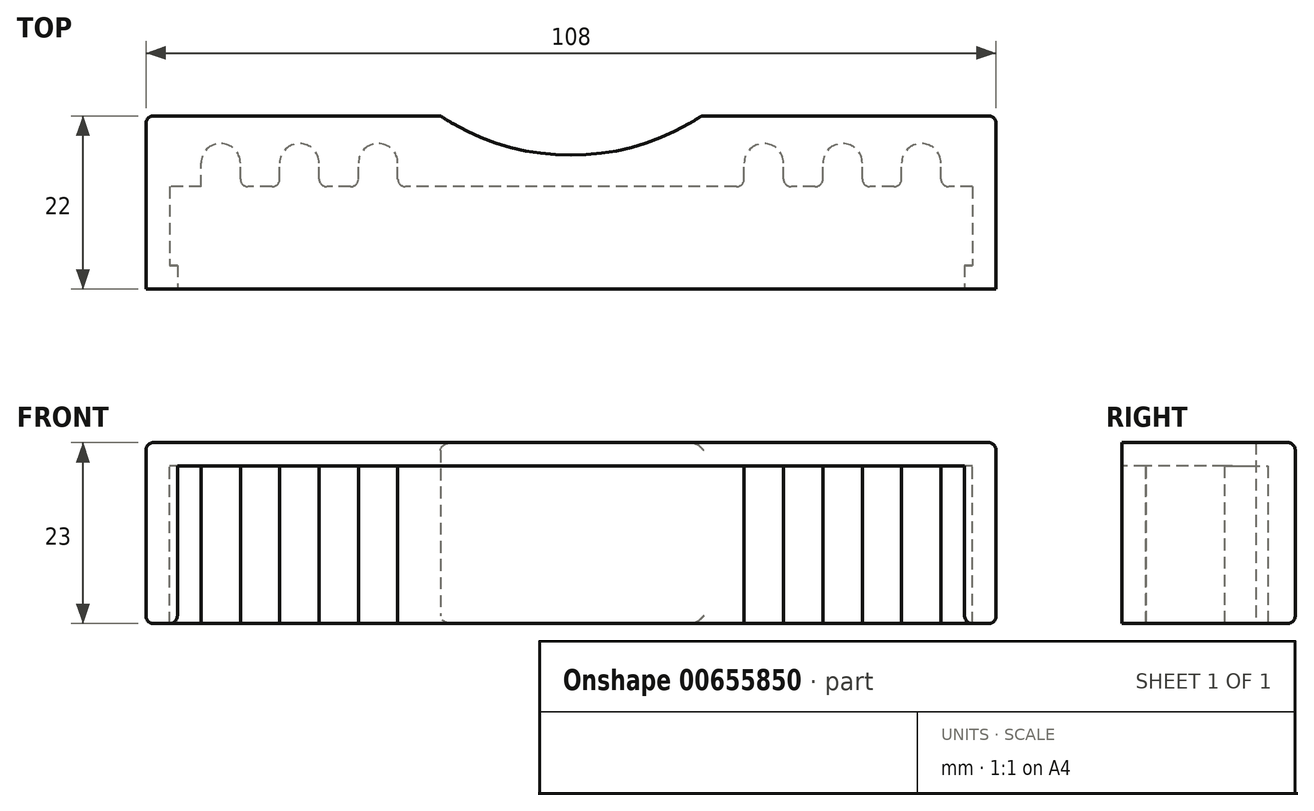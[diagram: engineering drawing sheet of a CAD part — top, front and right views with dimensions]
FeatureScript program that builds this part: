
annotation { "Feature Type Name" : "Feature", "Feature Type Description" : "" }
export const myFeature = defineFeature(function(context is Context, id is Id, definition is map)
    precondition{}
    {
        {
            var Q0;
            Q0=qCreatedBy(makeId("Front.planeOp"),FACE);
            var sketch = newSketch(context, id + "F0", { "sketchPlane" : qUnion([Q0])});
            skLineSegment(sketch, "E0.bottom", {"start": v(51, 0) * mm, "end": v(-51, 0) * mm});
            skLineSegment(sketch, "E0.top", {"start": v(51, 20) * mm, "end": v(-51, 20) * mm});
            skLineSegment(sketch, "E0.left", {"start": v(51, 0) * mm, "end": v(51, 20) * mm});
            skLineSegment(sketch, "E0.right", {"start": v(-51, 0) * mm, "end": v(-51, 20) * mm});
            skPoint(sketch, "E0.middle", {"position": v(0, 10) * mm});
            skLineSegment(sketch, "E1", {"start": v(-50, 20) * mm, "end": v(-50, 0) * mm});
            skLineSegment(sketch, "E2", {"start": v(50, 20) * mm, "end": v(50, 0) * mm});
            skLineSegment(sketch, "E3.0", {"start": v(-54, 0) * mm, "end": v(-54, 23) * mm});
            skLineSegment(sketch, "E3.1", {"start": v(54, 23) * mm, "end": v(-54, 23) * mm});
            skLineSegment(sketch, "E3.2", {"start": v(54, 0) * mm, "end": v(54, 23) * mm});
            skLineSegment(sketch, "E4", {"start": v(-54, 0) * mm, "end": v(-51, 0) * mm});
            skLineSegment(sketch, "E5", {"start": v(51, 0) * mm, "end": v(54, 0) * mm});
            skSolve(sketch);
        }
        {
            var Q0;
            {var subQ0=sQuery(id+"F0.wireOp",EDGE,"E0.left");Q0=makeQuery(id+"F0.imprint","IMPRINT",FACE,{"disambiguationData":[TD([[makeQuery(id+"F0.imprint","IMPRINT",EDGE,{"derivedFrom":subQ0}),-1.0]])]});}
            var Q1;
            {var subQ0=sQuery(id+"F0.wireOp",EDGE,"E0.right");Q1=makeQuery(id+"F0.imprint","IMPRINT",FACE,{"disambiguationData":[TD([[makeQuery(id+"F0.imprint","IMPRINT",EDGE,{"derivedFrom":subQ0}),-1.0]])]});}
            var Q2;
            {var subQ0=sQuery(id+"F0.wireOp",EDGE,"E1");Q2=makeQuery(id+"F0.imprint","IMPRINT",FACE,{"disambiguationData":[TD([[makeQuery(id+"F0.imprint","IMPRINT",EDGE,{"derivedFrom":subQ0}),1.0]])]});}
            var Q3;
            {var subQ0=sQuery(id+"F0.wireOp",EDGE,"E0.left");Q3=makeQuery(id+"F0.imprint","IMPRINT",FACE,{"disambiguationData":[TD([[makeQuery(id+"F0.imprint","IMPRINT",EDGE,{"derivedFrom":subQ0}),1.0]])]});}
            extrude(context, id + "F1", {"entities" : qUnion([Q0, Q1, Q2, Q3]), "oppositeDirection" : true, "depth" : 22 * mm, "offsetDistance" : 25 * mm});
        }
        {
            var Q0;
            {var subQ0=sQuery(id+"F0.wireOp",EDGE,"E0.right");Q0=makeQuery(id+"F0.imprint","IMPRINT",FACE,{"disambiguationData":[TD([[makeQuery(id+"F0.imprint","IMPRINT",EDGE,{"derivedFrom":subQ0}),-1.0]])]});}
            var Q1;
            {var subQ0=sQuery(id+"F0.wireOp",EDGE,"E1");Q1=makeQuery(id+"F0.imprint","IMPRINT",FACE,{"disambiguationData":[TD([[makeQuery(id+"F0.imprint","IMPRINT",EDGE,{"derivedFrom":subQ0}),1.0]])]});}
            var Q2;
            {var subQ0=sQuery(id+"F0.wireOp",EDGE,"E0.left");Q2=makeQuery(id+"F0.imprint","IMPRINT",FACE,{"disambiguationData":[TD([[makeQuery(id+"F0.imprint","IMPRINT",EDGE,{"derivedFrom":subQ0}),1.0]])]});}
            extrude(context, id + "F2", {"entities" : qUnion([Q0, Q1, Q2]), "operationType" : NewBodyOperationType.REMOVE, "oppositeDirection" : true, "depth" : 13 * mm, "offsetDistance" : 25 * mm});
        }
        {
            var Q0;
            {var subQ0=sQuery(id+"F0.wireOp",EDGE,"E0.right");Q0=makeQuery(id+"F0.imprint","IMPRINT",FACE,{"disambiguationData":[TD([[makeQuery(id+"F0.imprint","IMPRINT",EDGE,{"derivedFrom":subQ0}),-1.0]])]});}
            var Q1;
            {var subQ0=sQuery(id+"F0.wireOp",EDGE,"E0.left");Q1=makeQuery(id+"F0.imprint","IMPRINT",FACE,{"disambiguationData":[TD([[makeQuery(id+"F0.imprint","IMPRINT",EDGE,{"derivedFrom":subQ0}),1.0]])]});}
            extrude(context, id + "F3", {"entities" : qUnion([Q0, Q1]), "operationType" : NewBodyOperationType.ADD, "oppositeDirection" : true, "depth" : 3 * mm, "offsetDistance" : 25 * mm});
        }
        {
            var Q0;
            {var subQ0=sQuery(id+"F0.wireOp",EDGE,"E4");var subQ1=sQuery(id+"F0.wireOp",EDGE,"E0.bottom");var subQ2=sQuery(id+"F0.wireOp",EDGE,"E5");Q0=makeQuery(id+"F3.boolean.opBoolean","MERGE",FACE,{"derivedFrom":[makeQuery(id+"F1.opExtrude","SWEPT_FACE",FACE,{"disambiguationData":[OSD([subQ1,subQ0,subQ2])]}),makeQuery(id+"F3.opExtrude","SWEPT_FACE",FACE,{"disambiguationData":[OSD([subQ1]),TDD([makeQuery(id+"F0.imprint","IMPRINT",EDGE,{"disambiguationData":[TD([[makeQuery(id+"F0.imprint","INTERSECT",VERTEX,{"derivedFrom":[subQ1,sQuery(id+"F0.wireOp",EDGE,"E2")]}),1.0]])],"derivedFrom":subQ1})])]}),makeQuery(id+"F3.opExtrude","SWEPT_FACE",FACE,{"disambiguationData":[OSD([subQ1]),TDD([makeQuery(id+"F0.imprint","IMPRINT",EDGE,{"disambiguationData":[TD([[makeQuery(id+"F0.imprint","INTERSECT",VERTEX,{"derivedFrom":[subQ1,sQuery(id+"F0.wireOp",EDGE,"E1")]}),-1.0]])],"derivedFrom":subQ1})])]})]});}
            var sketch = newSketch(context, id + "F4", { "sketchPlane" : qUnion([Q0])});
            skArc(sketch, "E6", {"start": v(16.58, -22) * mm, "mid": v(0, -17) * mm, "end": v(-16.58, -22) * mm});
            skLineSegment(sketch, "E7", {"start": v(0, -47) * mm, "end": v(0, 0) * mm, "construction": true});
            skLineSegment(sketch, "E8.bottom", {"start": v(-47, -13) * mm, "end": v(-42, -13) * mm});
            skLineSegment(sketch, "E8.top", {"start": v(-47, -16) * mm, "end": v(-42, -16) * mm});
            skLineSegment(sketch, "E8.left", {"start": v(-47, -13) * mm, "end": v(-47, -16) * mm});
            skLineSegment(sketch, "E8.right", {"start": v(-42, -13) * mm, "end": v(-42, -16) * mm});
            skLineSegment(sketch, "E9.bottom", {"start": v(-37, -13) * mm, "end": v(-32, -13) * mm});
            skLineSegment(sketch, "E9.top", {"start": v(-37, -16) * mm, "end": v(-32, -16) * mm});
            skLineSegment(sketch, "E9.left", {"start": v(-37, -13) * mm, "end": v(-37, -16) * mm});
            skLineSegment(sketch, "E9.right", {"start": v(-32, -13) * mm, "end": v(-32, -16) * mm});
            skLineSegment(sketch, "E10.bottom", {"start": v(-27, -13) * mm, "end": v(-22, -13) * mm});
            skLineSegment(sketch, "E10.top", {"start": v(-27, -16) * mm, "end": v(-22, -16) * mm});
            skLineSegment(sketch, "E10.left", {"start": v(-27, -13) * mm, "end": v(-27, -16) * mm});
            skLineSegment(sketch, "E10.right", {"start": v(-22, -13) * mm, "end": v(-22, -16) * mm});
            skLineSegment(sketch, "E11.MirrorCS", {"start": v(47, -16) * mm, "end": v(42, -16) * mm});
            skLineSegment(sketch, "E12.MirrorCS", {"start": v(27, -13) * mm, "end": v(27, -16) * mm});
            skLineSegment(sketch, "E13.MirrorCS", {"start": v(27, -13) * mm, "end": v(22, -13) * mm});
            skLineSegment(sketch, "E14.MirrorCS", {"start": v(37, -13) * mm, "end": v(32, -13) * mm});
            skLineSegment(sketch, "E15.MirrorCS", {"start": v(37, -13) * mm, "end": v(37, -16) * mm});
            skLineSegment(sketch, "E16.MirrorCS", {"start": v(22, -13) * mm, "end": v(22, -16) * mm});
            skLineSegment(sketch, "E17.MirrorCS", {"start": v(32, -13) * mm, "end": v(32, -16) * mm});
            skLineSegment(sketch, "E18.MirrorCS", {"start": v(27, -16) * mm, "end": v(22, -16) * mm});
            skLineSegment(sketch, "E19.MirrorCS", {"start": v(47, -13) * mm, "end": v(42, -13) * mm});
            skLineSegment(sketch, "E20.MirrorCS", {"start": v(42, -13) * mm, "end": v(42, -16) * mm});
            skLineSegment(sketch, "E21.MirrorCS", {"start": v(37, -16) * mm, "end": v(32, -16) * mm});
            skLineSegment(sketch, "E22.MirrorCS", {"start": v(47, -13) * mm, "end": v(47, -16) * mm});
            skArc(sketch, "E23", {"start": v(-47, -16) * mm, "mid": v(-44.5, -18.5) * mm, "end": v(-42, -16) * mm});
            skArc(sketch, "E24", {"start": v(-37, -16) * mm, "mid": v(-34.5, -18.5) * mm, "end": v(-32, -16) * mm});
            skArc(sketch, "E25", {"start": v(-27, -16) * mm, "mid": v(-24.5, -18.5) * mm, "end": v(-22, -16) * mm});
            skArc(sketch, "E26.MirrorCS", {"start": v(27, -16) * mm, "mid": v(24.5, -18.5) * mm, "end": v(22, -16) * mm});
            skArc(sketch, "E27.MirrorCS", {"start": v(37, -16) * mm, "mid": v(34.5, -18.5) * mm, "end": v(32, -16) * mm});
            skArc(sketch, "E28.MirrorCS", {"start": v(47, -16) * mm, "mid": v(44.5, -18.5) * mm, "end": v(42, -16) * mm});
            skSolve(sketch);
        }
        {
            var Q0;
            {var subQ0=sQuery(id+"F4.wireOp",EDGE,"E6");Q0=makeQuery(id+"F4.imprint","IMPRINT",FACE,{"disambiguationData":[TD([[makeQuery(id+"F4.imprint","IMPRINT",EDGE,{"derivedFrom":subQ0}),1.0]])]});}
            var Q1;
            Q1=makeQuery(id+"F1.opExtrude","SWEPT_FACE",FACE,{"disambiguationData":[OSD([sQuery(id+"F0.wireOp",EDGE,"E3.1")])]});
            extrude(context, id + "F5", {"entities" : qUnion([Q0]), "operationType" : NewBodyOperationType.REMOVE, "endBound" : BoundingType.UP_TO_SURFACE, "oppositeDirection" : true, "depth" : 25 * mm, "endBoundEntityFace" : qUnion([Q1]), "offsetDistance" : 25 * mm});
        }
        {
            var Q0;
            Q0=makeQuery(id+"F4.imprint","IMPRINT",FACE,{"disambiguationData":[TD([[makeQuery(id+"F4.imprint","IMPRINT",EDGE,{"derivedFrom":sQuery(id+"F4.wireOp",EDGE,"E8.bottom")}),1.0]])]});
            var Q1;
            Q1=makeQuery(id+"F4.imprint","IMPRINT",FACE,{"disambiguationData":[TD([[makeQuery(id+"F4.imprint","IMPRINT",EDGE,{"derivedFrom":sQuery(id+"F4.wireOp",EDGE,"E9.bottom")}),1.0]])]});
            var Q2;
            Q2=makeQuery(id+"F4.imprint","IMPRINT",FACE,{"disambiguationData":[TD([[makeQuery(id+"F4.imprint","IMPRINT",EDGE,{"derivedFrom":sQuery(id+"F4.wireOp",EDGE,"E10.bottom")}),1.0]])]});
            var Q3;
            Q3=makeQuery(id+"F4.imprint","IMPRINT",FACE,{"disambiguationData":[TD([[makeQuery(id+"F4.imprint","IMPRINT",EDGE,{"derivedFrom":sQuery(id+"F4.wireOp",EDGE,"E12.MirrorCS")}),-1.0]])]});
            var Q4;
            Q4=makeQuery(id+"F4.imprint","IMPRINT",FACE,{"disambiguationData":[TD([[makeQuery(id+"F4.imprint","IMPRINT",EDGE,{"derivedFrom":sQuery(id+"F4.wireOp",EDGE,"E14.MirrorCS")}),1.0]])]});
            var Q5;
            Q5=makeQuery(id+"F4.imprint","IMPRINT",FACE,{"disambiguationData":[TD([[makeQuery(id+"F4.imprint","IMPRINT",EDGE,{"derivedFrom":sQuery(id+"F4.wireOp",EDGE,"E11.MirrorCS")}),-1.0]])]});
            var Q6;
            Q6=makeQuery(id+"F4.imprint","IMPRINT",FACE,{"disambiguationData":[TD([[makeQuery(id+"F4.imprint","IMPRINT",EDGE,{"derivedFrom":sQuery(id+"F4.wireOp",EDGE,"E8.top")}),-1.0]])]});
            var Q7;
            Q7=makeQuery(id+"F4.imprint","IMPRINT",FACE,{"disambiguationData":[TD([[makeQuery(id+"F4.imprint","IMPRINT",EDGE,{"derivedFrom":sQuery(id+"F4.wireOp",EDGE,"E9.top")}),-1.0]])]});
            var Q8;
            Q8=makeQuery(id+"F4.imprint","IMPRINT",FACE,{"disambiguationData":[TD([[makeQuery(id+"F4.imprint","IMPRINT",EDGE,{"derivedFrom":sQuery(id+"F4.wireOp",EDGE,"E10.top")}),-1.0]])]});
            var Q9;
            Q9=makeQuery(id+"F4.imprint","IMPRINT",FACE,{"disambiguationData":[TD([[makeQuery(id+"F4.imprint","IMPRINT",EDGE,{"derivedFrom":sQuery(id+"F4.wireOp",EDGE,"E18.MirrorCS")}),1.0]])]});
            var Q10;
            Q10=makeQuery(id+"F4.imprint","IMPRINT",FACE,{"disambiguationData":[TD([[makeQuery(id+"F4.imprint","IMPRINT",EDGE,{"derivedFrom":sQuery(id+"F4.wireOp",EDGE,"E21.MirrorCS")}),1.0]])]});
            var Q11;
            Q11=makeQuery(id+"F4.imprint","IMPRINT",FACE,{"disambiguationData":[TD([[makeQuery(id+"F4.imprint","IMPRINT",EDGE,{"derivedFrom":sQuery(id+"F4.wireOp",EDGE,"E11.MirrorCS")}),1.0]])]});
            var Q12;
            Q12=makeQuery(id+"F2.boolean.opBoolean","COPY",FACE,{"derivedFrom":makeQuery(id+"F2.opExtrude","SWEPT_FACE",FACE,{"disambiguationData":[OSD([sQuery(id+"F0.wireOp",EDGE,"E0.top")])]})});
            extrude(context, id + "F6", {"entities" : qUnion([Q0, Q1, Q2, Q3, Q4, Q5, Q6, Q7, Q8, Q9, Q10, Q11]), "operationType" : NewBodyOperationType.REMOVE, "endBound" : BoundingType.UP_TO_SURFACE, "oppositeDirection" : true, "depth" : 25 * mm, "endBoundEntityFace" : qUnion([Q12]), "offsetDistance" : 25 * mm});
        }
        {
            var Q0;
            Q0=makeQuery(id+"F1.opExtrude","CAP_EDGE",EDGE,{"disambiguationData":[OSD([sQuery(id+"F0.wireOp",EDGE,"E3.0")])],"isStart":false});
            var Q1;
            Q1=makeQuery(id+"F1.opExtrude","CAP_EDGE",EDGE,{"disambiguationData":[OSD([sQuery(id+"F0.wireOp",EDGE,"E3.2")])],"isStart":false});
            var Q2;
            Q2=makeQuery(id+"F1.opExtrude","CAP_EDGE",EDGE,{"disambiguationData":[OSD([sQuery(id+"F0.wireOp",EDGE,"E0.bottom"),sQuery(id+"F0.wireOp",EDGE,"E4"),sQuery(id+"F0.wireOp",EDGE,"E5")])],"isStart":false});
            var Q3;
            Q3=makeQuery(id+"F1.opExtrude","SWEPT_EDGE",EDGE,{"disambiguationData":[OSD([sQuery(id+"F0.wireOp",EDGE,"E3.2"),sQuery(id+"F0.wireOp",EDGE,"E5")])]});
            var Q4;
            Q4=makeQuery(id+"F1.opExtrude","SWEPT_EDGE",EDGE,{"disambiguationData":[OSD([sQuery(id+"F0.wireOp",EDGE,"E3.0"),sQuery(id+"F0.wireOp",EDGE,"E4")])]});
            var Q5;
            Q5=makeQuery(id+"F1.opExtrude","SWEPT_EDGE",EDGE,{"disambiguationData":[OSD([sQuery(id+"F0.wireOp",EDGE,"E3.0"),sQuery(id+"F0.wireOp",EDGE,"E3.1")])]});
            var Q6;
            Q6=makeQuery(id+"F1.opExtrude","CAP_EDGE",EDGE,{"disambiguationData":[OSD([sQuery(id+"F0.wireOp",EDGE,"E3.1")])],"isStart":false});
            var Q7;
            Q7=makeQuery(id+"F1.opExtrude","SWEPT_EDGE",EDGE,{"disambiguationData":[OSD([sQuery(id+"F0.wireOp",EDGE,"E3.1"),sQuery(id+"F0.wireOp",EDGE,"E3.2")])]});
            var Q8;
            Q8=makeQuery(id+"F2.boolean.opBoolean","COPY",EDGE,{"derivedFrom":makeQuery(id+"F2.opExtrude","CAP_EDGE",EDGE,{"disambiguationData":[OSD([sQuery(id+"F0.wireOp",EDGE,"E0.bottom")])],"isStart":false})});
            var Q9;
            Q9=makeQuery(id+"F2.boolean.opBoolean","COPY",EDGE,{"derivedFrom":makeQuery(id+"F2.opExtrude","SWEPT_EDGE",EDGE,{"disambiguationData":[OSD([sQuery(id+"F0.wireOp",EDGE,"E0.bottom"),sQuery(id+"F0.wireOp",EDGE,"E0.left"),sQuery(id+"F0.wireOp",EDGE,"E5")])]})});
            var Q10;
            Q10=makeQuery(id+"F2.boolean.opBoolean","COPY",EDGE,{"derivedFrom":makeQuery(id+"F2.opExtrude","SWEPT_EDGE",EDGE,{"disambiguationData":[OSD([sQuery(id+"F0.wireOp",EDGE,"E0.bottom"),sQuery(id+"F0.wireOp",EDGE,"E0.right"),sQuery(id+"F0.wireOp",EDGE,"E4")])]})});
            var Q11;
            Q11=makeQuery(id+"F3.opExtrude","SWEPT_EDGE",EDGE,{"disambiguationData":[OSD([sQuery(id+"F0.wireOp",EDGE,"E0.bottom"),sQuery(id+"F0.wireOp",EDGE,"E1")])]});
            var Q12;
            Q12=makeQuery(id+"F3.opExtrude","SWEPT_EDGE",EDGE,{"disambiguationData":[OSD([sQuery(id+"F0.wireOp",EDGE,"E0.bottom"),sQuery(id+"F0.wireOp",EDGE,"E2")])]});
            var Q13;
            Q13=makeQuery(id+"F5.boolean.opBoolean","COPY",EDGE,{"derivedFrom":makeQuery(id+"F5.opExtrude","CAP_EDGE",EDGE,{"disambiguationData":[OSD([sQuery(id+"F4.wireOp",EDGE,"U0nTRzHa-0Nyo-Q8gQ-bPhF-44hzxR5yK4Ol")])],"isStart":false})});
            var Q14;
            Q14=makeQuery(id+"F5.boolean.opBoolean","COPY",EDGE,{"derivedFrom":makeQuery(id+"F5.opExtrude","CAP_EDGE",EDGE,{"disambiguationData":[OSD([sQuery(id+"F4.wireOp",EDGE,"E6")])],"isStart":false})});
            var Q15;
            {var subQ0=sQuery(id+"F4.wireOp",EDGE,"b88245b2-9b70-4256-9dea-91accad25118.9.17.0");var subQ1=sQuery(id+"F4.wireOp",EDGE,"U0nTRzHa-0Nyo-Q8gQ-bPhF-44hzxR5yK4Ol");Q15=makeQuery(id+"F5.boolean.opBoolean","COPY",EDGE,{"derivedFrom":makeQuery(id+"F5.opExtrude","SWEPT_EDGE",EDGE,{"disambiguationData":[OSD([subQ1,subQ0]),TDD([makeQuery(id+"F4.imprint","INTERSECT",VERTEX,{"disambiguationData":[OD(0.0)],"derivedFrom":[subQ1,subQ0]})])]})});}
            var Q16;
            Q16=makeQuery(id+"F5.boolean.opBoolean","COPY",EDGE,{"derivedFrom":makeQuery(id+"F5.opExtrude","SWEPT_EDGE",EDGE,{"disambiguationData":[OSD([sQuery(id+"F4.wireOp",EDGE,"E6"),sQuery(id+"F4.wireOp",EDGE,"b88245b2-9b70-4256-9dea-91accad25118.9.17.0")])]})});
            var Q17;
            Q17=makeQuery(id+"F5.boolean.opBoolean","COPY",EDGE,{"derivedFrom":makeQuery(id+"F5.opExtrude","CAP_EDGE",EDGE,{"disambiguationData":[OSD([sQuery(id+"F4.wireOp",EDGE,"E6")])],"isStart":true})});
            var Q18;
            Q18=makeQuery(id+"F5.boolean.opBoolean","COPY",EDGE,{"derivedFrom":makeQuery(id+"F5.opExtrude","CAP_EDGE",EDGE,{"disambiguationData":[OSD([sQuery(id+"F4.wireOp",EDGE,"U0nTRzHa-0Nyo-Q8gQ-bPhF-44hzxR5yK4Ol")])],"isStart":true})});
            var Q19;
            {var subQ0=sQuery(id+"F4.wireOp",EDGE,"b88245b2-9b70-4256-9dea-91accad25118.9.17.0");var subQ1=sQuery(id+"F4.wireOp",EDGE,"U0nTRzHa-0Nyo-Q8gQ-bPhF-44hzxR5yK4Ol");Q19=makeQuery(id+"F5.boolean.opBoolean","COPY",EDGE,{"derivedFrom":makeQuery(id+"F5.opExtrude","SWEPT_EDGE",EDGE,{"disambiguationData":[OSD([subQ1,subQ0]),TDD([makeQuery(id+"F4.imprint","INTERSECT",VERTEX,{"disambiguationData":[OD(1.0)],"derivedFrom":[subQ1,subQ0]})])]})});}
            var Q20;
            Q20=makeQuery(id+"F5.boolean.opBoolean","COPY",EDGE,{"derivedFrom":makeQuery(id+"F5.opExtrude","SWEPT_EDGE",EDGE,{"disambiguationData":[OSD([sQuery(id+"F4.wireOp",EDGE,"E6"),sQuery(id+"F4.wireOp",EDGE,"3e7a33aa-6f93-4459-9776-8ad97c84258c.9.3.0")])]})});
            var Q21;
            Q21=makeQuery(id+"F6.boolean.opBoolean","COPY",EDGE,{"derivedFrom":makeQuery(id+"F6.opExtrude","SWEPT_EDGE",EDGE,{"disambiguationData":[OSD([sQuery(id+"F0.wireOp",EDGE,"E0.bottom"),sQuery(id+"F4.wireOp",EDGE,"E8.bottom"),sQuery(id+"F4.wireOp",EDGE,"E8.left")])]})});
            var Q22;
            Q22=makeQuery(id+"F6.boolean.opBoolean","COPY",EDGE,{"derivedFrom":makeQuery(id+"F6.opExtrude","SWEPT_EDGE",EDGE,{"disambiguationData":[OSD([sQuery(id+"F0.wireOp",EDGE,"E0.bottom"),sQuery(id+"F4.wireOp",EDGE,"E8.bottom"),sQuery(id+"F4.wireOp",EDGE,"E8.right")])]})});
            var Q23;
            Q23=makeQuery(id+"F6.boolean.opBoolean","COPY",EDGE,{"derivedFrom":makeQuery(id+"F6.opExtrude","SWEPT_EDGE",EDGE,{"disambiguationData":[OSD([sQuery(id+"F0.wireOp",EDGE,"E0.bottom"),sQuery(id+"F4.wireOp",EDGE,"E9.bottom"),sQuery(id+"F4.wireOp",EDGE,"E9.left")])]})});
            var Q24;
            Q24=makeQuery(id+"F6.boolean.opBoolean","COPY",EDGE,{"derivedFrom":makeQuery(id+"F6.opExtrude","SWEPT_EDGE",EDGE,{"disambiguationData":[OSD([sQuery(id+"F0.wireOp",EDGE,"E0.bottom"),sQuery(id+"F4.wireOp",EDGE,"E9.bottom"),sQuery(id+"F4.wireOp",EDGE,"E9.right")])]})});
            var Q25;
            Q25=makeQuery(id+"F6.boolean.opBoolean","COPY",EDGE,{"derivedFrom":makeQuery(id+"F6.opExtrude","SWEPT_EDGE",EDGE,{"disambiguationData":[OSD([sQuery(id+"F0.wireOp",EDGE,"E0.bottom"),sQuery(id+"F4.wireOp",EDGE,"E10.bottom"),sQuery(id+"F4.wireOp",EDGE,"E10.left")])]})});
            var Q26;
            Q26=makeQuery(id+"F6.boolean.opBoolean","COPY",EDGE,{"derivedFrom":makeQuery(id+"F6.opExtrude","SWEPT_EDGE",EDGE,{"disambiguationData":[OSD([sQuery(id+"F0.wireOp",EDGE,"E0.bottom"),sQuery(id+"F4.wireOp",EDGE,"E10.bottom"),sQuery(id+"F4.wireOp",EDGE,"E10.right")])]})});
            var Q27;
            Q27=makeQuery(id+"F6.boolean.opBoolean","COPY",EDGE,{"derivedFrom":makeQuery(id+"F6.opExtrude","SWEPT_EDGE",EDGE,{"disambiguationData":[OSD([sQuery(id+"F0.wireOp",EDGE,"E0.bottom"),sQuery(id+"F4.wireOp",EDGE,"E13.MirrorCS"),sQuery(id+"F4.wireOp",EDGE,"E16.MirrorCS")])]})});
            var Q28;
            Q28=makeQuery(id+"F6.boolean.opBoolean","COPY",EDGE,{"derivedFrom":makeQuery(id+"F6.opExtrude","SWEPT_EDGE",EDGE,{"disambiguationData":[OSD([sQuery(id+"F0.wireOp",EDGE,"E0.bottom"),sQuery(id+"F4.wireOp",EDGE,"E12.MirrorCS"),sQuery(id+"F4.wireOp",EDGE,"E13.MirrorCS")])]})});
            var Q29;
            Q29=makeQuery(id+"F6.boolean.opBoolean","COPY",EDGE,{"derivedFrom":makeQuery(id+"F6.opExtrude","SWEPT_EDGE",EDGE,{"disambiguationData":[OSD([sQuery(id+"F0.wireOp",EDGE,"E0.bottom"),sQuery(id+"F4.wireOp",EDGE,"E14.MirrorCS"),sQuery(id+"F4.wireOp",EDGE,"E17.MirrorCS")])]})});
            var Q30;
            Q30=makeQuery(id+"F6.boolean.opBoolean","COPY",EDGE,{"derivedFrom":makeQuery(id+"F6.opExtrude","SWEPT_EDGE",EDGE,{"disambiguationData":[OSD([sQuery(id+"F0.wireOp",EDGE,"E0.bottom"),sQuery(id+"F4.wireOp",EDGE,"E19.MirrorCS"),sQuery(id+"F4.wireOp",EDGE,"E22.MirrorCS")])]})});
            var Q31;
            Q31=makeQuery(id+"F6.boolean.opBoolean","COPY",EDGE,{"derivedFrom":makeQuery(id+"F6.opExtrude","SWEPT_EDGE",EDGE,{"disambiguationData":[OSD([sQuery(id+"F0.wireOp",EDGE,"E0.bottom"),sQuery(id+"F4.wireOp",EDGE,"E19.MirrorCS"),sQuery(id+"F4.wireOp",EDGE,"E20.MirrorCS")])]})});
            var Q32;
            Q32=makeQuery(id+"F6.boolean.opBoolean","COPY",EDGE,{"derivedFrom":makeQuery(id+"F6.opExtrude","SWEPT_EDGE",EDGE,{"disambiguationData":[OSD([sQuery(id+"F0.wireOp",EDGE,"E0.bottom"),sQuery(id+"F4.wireOp",EDGE,"E14.MirrorCS"),sQuery(id+"F4.wireOp",EDGE,"E15.MirrorCS")])]})});
            fillet(context, id + "F7", {"entities" : qUnion([Q0, Q1, Q2, Q3, Q4, Q5, Q6, Q7, Q8, Q9, Q10, Q11, Q12, Q13, Q14, Q15, Q16, Q17, Q18, Q19, Q20, Q21, Q22, Q23, Q24, Q25, Q26, Q27, Q28, Q29, Q30, Q31, Q32]), "radius" : 1 * mm, "tangentPropagation" : true, "defaultsChanged" : false, "vertexSettings" : [], "allowEdgeOverflow" : false});
        }
    });
